# Revit family: P191568KX-105c_KOWT100E
name_source: partatom
category: Specialty Equipment
units: mm (PartAtom-declared; Revit-internal decimal feet)

## family parameters
Always vertical = Yes
Cut with Voids When Loaded = No
Enable Cutting in Views = No
Maintain Annotation Orientation = No
Part Type = Normal
Room Calculation Point = No
Round Connector Dimension = Use Diameter
Shared = No
Work Plane-Based = No

## types (1)
- KOWT100ESS
    Amps = 15 A
    Body Material = ARCAT - Metal - Steel - Stainless
    Clearance Material = ARCAT - Clearance
    Default Elevation = 0"
    Depth = 26"
    Description = 30'' Slow Cook Warming Drawer
Tiroir-réchaud et mijoteuse de 30 po
    Dimension Guide = http://access.whirlpool.com Guide&sku=KOWT100ESS&language=EN
http://access.whirlpool.com Guide&sku=KOWT100ESS&language=EN
    Door Panel Material = ARCAT - Metal - Steel - Stainless
    Family Name = COOKING
    Feature 1 = Slow Cook Function
Fonction de mijotage
    Feature 2 = Bread Proofing
Levage de pain
    Feature 3 = Humidity Slide Control
Commande coulissante de contrôle d'humidité
    Handle Material = ARCAT - Metal - Steel - Gray
    Height = 10 1/4"
    Installation-Fabrication = http://access.whirlpool.com Instruction&sku=KOWT100ESS&language=EN
http://access.whirlpool.com Instruction&sku=KOWT100ESS&language=FR
    Manufacturer = KitchenAid
    Model = KOWT100ESS
    Voltage = 120 V
    Width = 29 3/4"

## geometry (parser evidence)
native form markers: Sweep x6
no freeform markers — native parametric forms only
